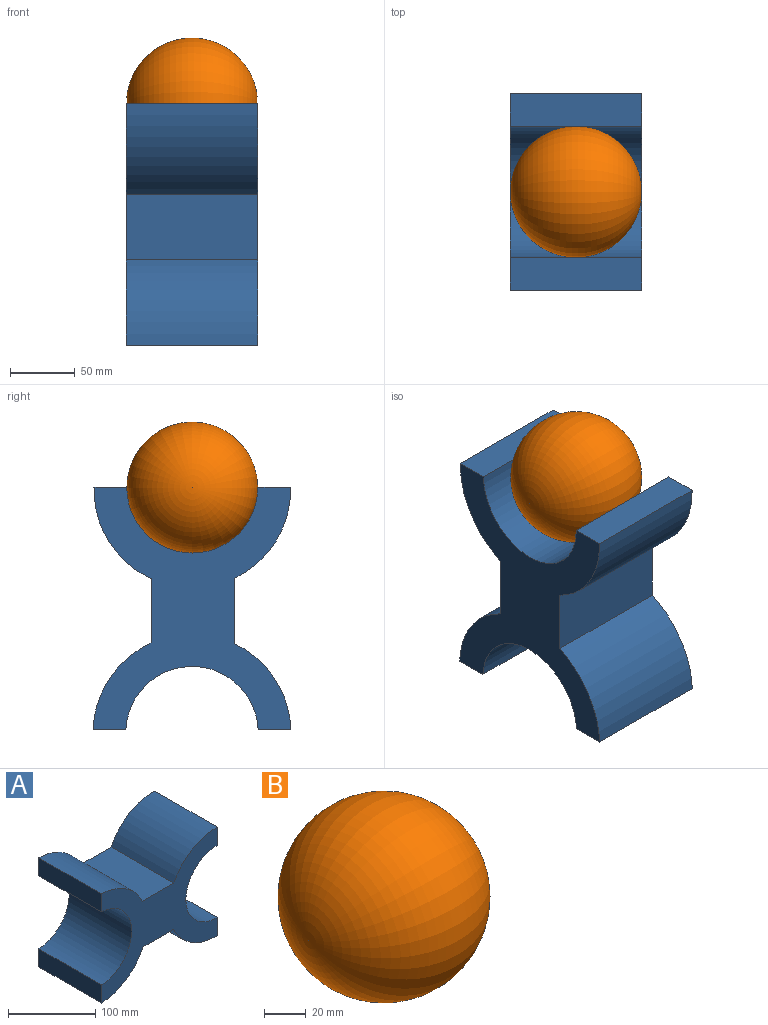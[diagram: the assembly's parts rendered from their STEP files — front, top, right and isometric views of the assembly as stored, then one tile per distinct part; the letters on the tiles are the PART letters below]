
ASSEMBLY  parts=2 mates=1
PART A: 14 faces, bbox 188x101.6x153.3 mm
  f0: plane 101.6x25.4mm, normal (-1,0,0), area 2580.6mm2, adj f1,f11,f12,f13
  f1: cylinder r=76.71mm len=101.6mm, axis (0,1,0), area 8654.1mm2, adj f0,f2,f12,f13
  f2: plane 101.6x49.79mm, normal (0,0,-1), area 5058.5mm2, adj f1,f3,f12,f13
  f3: cylinder r=76.22mm len=101.6mm, axis (0,1,0), area 8980.9mm2, adj f2,f4,f12,f13
  f4: plane 101.6x25.4mm, normal (1,0,0), area 2580.6mm2, adj f3,f5,f12,f13
  f5: cylinder r=50.8mm len=101.6mm, axis (0,1,0), area 16244.3mm2, adj f4,f6,f12,f13
  f6: plane 101.6x25.4mm, normal (1,0,0), area 2580.6mm2, adj f5,f7,f12,f13
  f7: cylinder r=76.22mm len=101.6mm, axis (0,1,0), area 8884.9mm2, adj f6,f8,f12,f13
  f8: plane 101.6x50.8mm, normal (0,0,1), area 5161.3mm2, adj f7,f9,f12,f13
  f9: cylinder r=76.71mm len=101.6mm, axis (0,1,0), area 8524.8mm2, adj f8,f10,f12,f13
  f10: plane 101.6x25.4mm, normal (-1,0,0), area 2580.6mm2, adj f9,f11,f12,f13
  f11: cylinder r=51.31mm len=102.53mm, axis (0,1,0), area 15932.7mm2, adj f0,f10,f12,f13
  f12: plane 188.03x153.33mm, normal (0,-1,0), area 12881mm2, adj f0,f1,f2,f3,f4,f5,f6,f7
  f13: plane 188.03x153.33mm, normal (0,1,0), area 12881mm2, adj f0,f1,f2,f3,f4,f5,f6,f7
PART B: 1 faces, bbox 101.6x0x50.8 mm
  f0: torus R=0.04mm, axis (-1,0,0), area 32390.1mm2
PLACE A rot(axis=(0.58,-0.58,0.58),120deg) t=(11.08,69.44,-60.76)mm
PLACE B t=(57.27,45.96,15.35)mm
MATE fastened A.f5 <-> B.f0  axis (-1,0,0) through (61.88,45.96,15.35)mm
